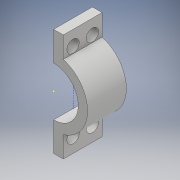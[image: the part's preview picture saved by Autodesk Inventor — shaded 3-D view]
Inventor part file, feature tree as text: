
AUTODESK INVENTOR PART (.ipt)
format: ipt  version: 2018 (Build 220112000, 112)  size: 151,552 bytes
history: native  units: mm
features: sketch x5, extrude x4
ambient origin geometry x8: Origin, YZ Plane, XZ Plane, XY Plane, X Axis, Y Axis, Z Axis, Center Point
bodies: Solid1 (feature_tree)
feature tree (9):
  extrude  "Extrusion1"  Depth=35.0mm
  extrude  "Extrusion2"  Depth=20.0mm TaperAngle=0.0deg
  sketch  "Sketch3"  dims[d6=15.0mm d7=15.0mm]
  sketch  "Sketch4"  dims[d8=5.0mm d9=0.0mm d10=6.35mm]
  extrude  "Extrusion3"  Depth=15.0mm
  extrude  "Extrusion4"  Depth=5.0mm
  sketch  "Sketch1"  dims[d0=25.4mm d1=35.0mm]
  sketch  "Sketch2"  dims[d2=20.0mm d3=0.0mm d4=20.0mm d5=0.0mm]
  sketch  "Sketch5"  dims[d11=6.35mm d12=6.35mm d13=6.35mm d14=6.35mm d15=5.0mm d16=0.0mm]
